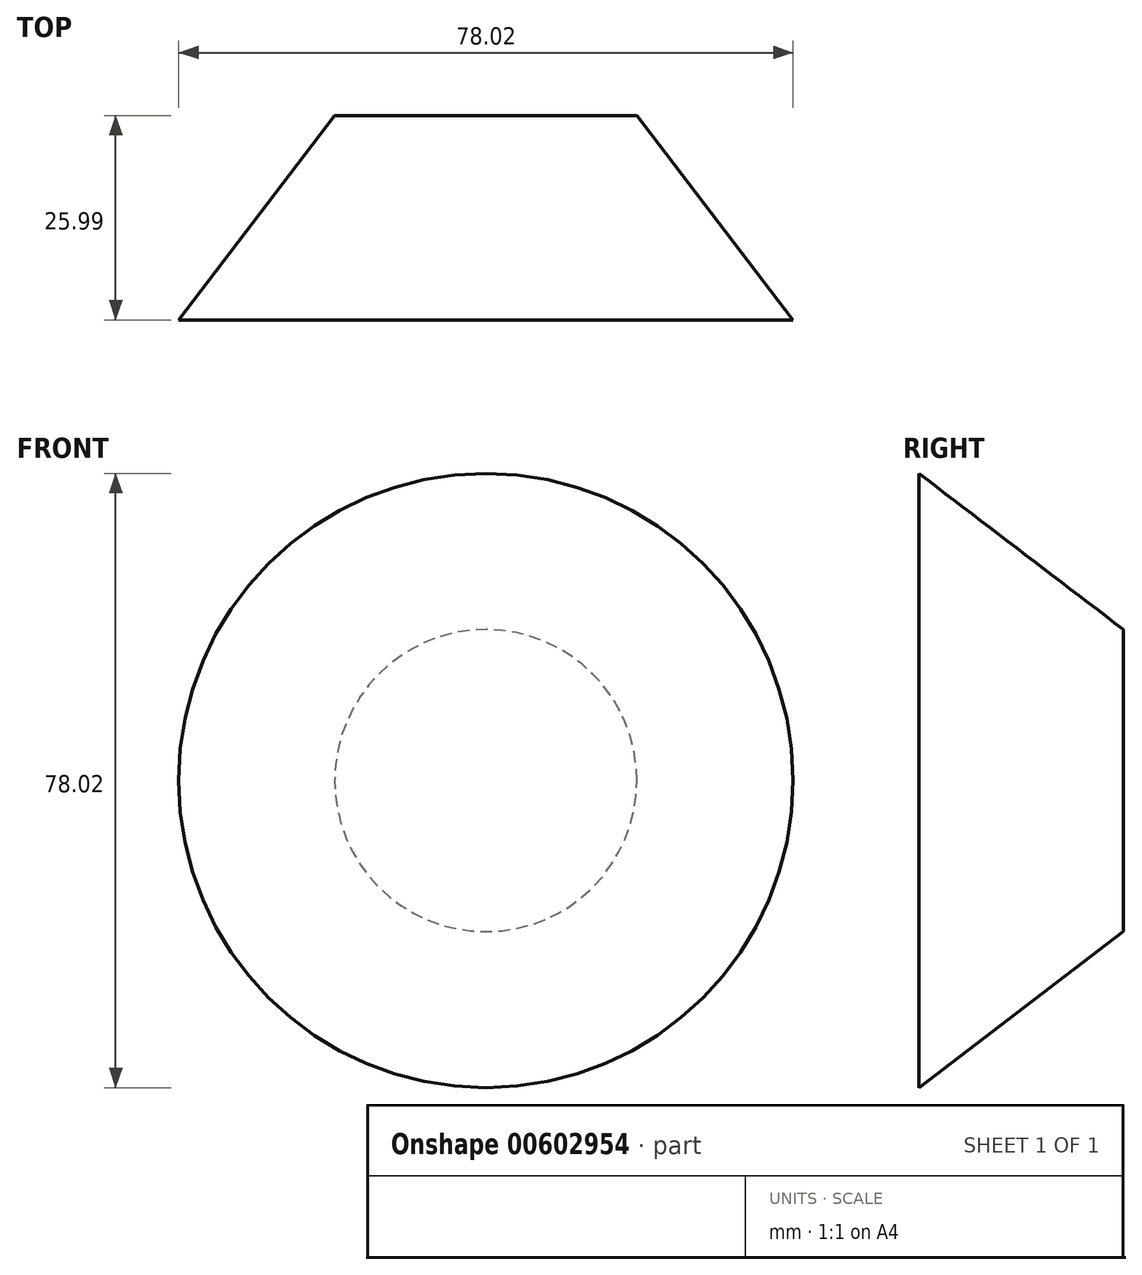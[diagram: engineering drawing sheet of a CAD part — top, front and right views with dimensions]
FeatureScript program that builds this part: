
annotation { "Feature Type Name" : "Feature", "Feature Type Description" : "" }
export const myFeature = defineFeature(function(context is Context, id is Id, definition is map)
    precondition{}
    {
        {
            var Q0;
            Q0=qCreatedBy(makeId("Top.planeOp"),FACE);
            var sketch = newSketch(context, id + "F0", { "sketchPlane" : qUnion([Q0])});
            skLineSegment(sketch, "E0", {"start": v(0, 25.99) * mm, "end": v(19.19, 25.99) * mm});
            skLineSegment(sketch, "E1", {"start": v(19.19, 25.99) * mm, "end": v(39.01, 0) * mm});
            skLineSegment(sketch, "E2", {"start": v(39.01, 0) * mm, "end": v(0, 0) * mm});
            skLineSegment(sketch, "E3", {"start": v(0, 25.99) * mm, "end": v(0, 0) * mm});
            skSolve(sketch);
        }
        {
            var Q0;
            Q0=makeQuery(id+"F0.imprint","IMPRINT",FACE,{"disambiguationData":[TD([[makeQuery(id+"F0.imprint","IMPRINT",EDGE,{"derivedFrom":sQuery(id+"F0.wireOp",EDGE,"E0")}),-1.0]])]});
            var Q1;
            Q1=sQuery(id+"F0.wireOp",EDGE,"E3");
            revolve(context, id + "F1", {"entities" : qUnion([Q0]), "axis" : qUnion([Q1]), "revolveType" : RevolveType.FULL});
        }
    });
